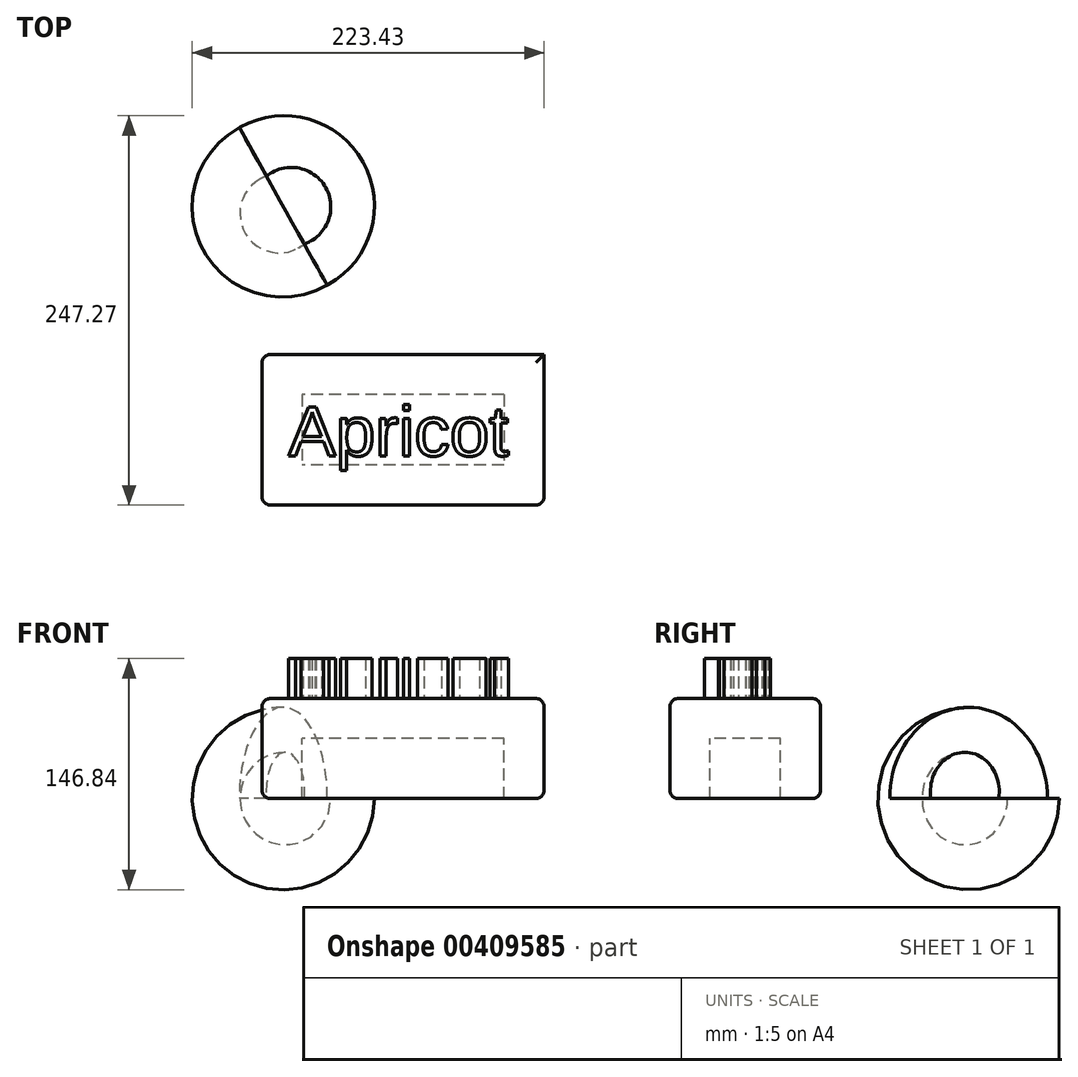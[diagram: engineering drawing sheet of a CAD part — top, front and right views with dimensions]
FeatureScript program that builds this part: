
annotation { "Feature Type Name" : "Feature", "Feature Type Description" : "" }
export const myFeature = defineFeature(function(context is Context, id is Id, definition is map)
    precondition{}
    {
        {
            var Q0;
            Q0=qCreatedBy(makeId("Top.planeOp"),FACE);
            var sketch = newSketch(context, id + "F0", { "sketchPlane" : qUnion([Q0])});
            skLineSegment(sketch, "E0.bottom", {"start": v(-97.09, -39.65) * mm, "end": v(81.91, -39.65) * mm});
            skLineSegment(sketch, "E0.top", {"start": v(-97.09, 55.98) * mm, "end": v(81.91, 55.98) * mm});
            skLineSegment(sketch, "E0.left", {"start": v(-97.09, -39.65) * mm, "end": v(-97.09, 55.98) * mm});
            skLineSegment(sketch, "E0.right", {"start": v(81.91, -39.65) * mm, "end": v(81.91, 55.98) * mm});
            skSolve(sketch);
        }
        {
            var Q0;
            Q0=makeQuery(id+"F0.imprint","IMPRINT",FACE,{"disambiguationData":[TD([[makeQuery(id+"F0.imprint","IMPRINT",EDGE,{"derivedFrom":sQuery(id+"F0.wireOp",EDGE,"E0.bottom")}),1.0]])]});
            extrude(context, id + "F1", {"entities" : qUnion([Q0]), "depth" : 63.5 * mm});
        }
        {
            var Q0;
            Q0=qCreatedBy(makeId("Top.planeOp"),FACE);
            var sketch = newSketch(context, id + "F2", { "sketchPlane" : qUnion([Q0])});
            skLineSegment(sketch, "E1", {"start": v(0, 0) * mm, "end": v(-111.55, 200.04) * mm});
            skArc(sketch, "E2", {"start": v(-55.78, 100.02) * mm, "mid": v(-33.06, 178.25) * mm, "end": v(-111.55, 200.04) * mm});
            skArc(sketch, "E3", {"start": v(-70.34, 126.14) * mm, "mid": v(-56.68, 161.99) * mm, "end": v(-94.36, 169.2) * mm});
            skSolve(sketch);
        }
        {
            var Q0;
            {var subQ0=sQuery(id+"F2.wireOp",EDGE,"E2");Q0=makeQuery(id+"F2.imprint","IMPRINT",FACE,{"disambiguationData":[TD([[makeQuery(id+"F2.imprint","IMPRINT",EDGE,{"derivedFrom":subQ0}),1.0]])]});}
            var Q1;
            Q1=sQuery(id+"F2.wireOp",EDGE,"E1");
            revolve(context, id + "F3", {"entities" : qUnion([Q0]), "axis" : qUnion([Q1]), "revolveType" : RevolveType.ONE_DIRECTION, "angle" : 270 * degree});
        }
        {
            var Q0;
            Q0=makeQuery(id+"F1.opExtrude","SWEPT_FACE",FACE,{"disambiguationData":[OSD([sQuery(id+"F0.wireOp",EDGE,"E0.bottom")])]});
            var Q1;
            Q1=makeQuery(id+"F1.opExtrude","SWEPT_FACE",FACE,{"disambiguationData":[OSD([sQuery(id+"F0.wireOp",EDGE,"E0.left")])]});
            var Q2;
            Q2=makeQuery(id+"F1.opExtrude","CAP_EDGE",EDGE,{"disambiguationData":[OSD([sQuery(id+"F0.wireOp",EDGE,"E0.right")])],"isStart":false});
            var Q3;
            Q3=makeQuery(id+"F1.opExtrude","CAP_FACE",FACE,{"disambiguationData":[OSD([sQuery(id+"F0.wireOp",EDGE,"E0.bottom"),sQuery(id+"F0.wireOp",EDGE,"E0.top"),sQuery(id+"F0.wireOp",EDGE,"E0.left"),sQuery(id+"F0.wireOp",EDGE,"E0.right")])],"isStart":false});
            var Q4;
            Q4=makeQuery(id+"F1.opExtrude","CAP_FACE",FACE,{"disambiguationData":[OSD([sQuery(id+"F0.wireOp",EDGE,"E0.bottom"),sQuery(id+"F0.wireOp",EDGE,"E0.top"),sQuery(id+"F0.wireOp",EDGE,"E0.left"),sQuery(id+"F0.wireOp",EDGE,"E0.right")])],"isStart":true});
            fillet(context, id + "F4", {"entities" : qUnion([Q0, Q1, Q2, Q3, Q4]), "radius" : 5.08 * mm, "tangentPropagation" : true, "allowEdgeOverflow" : false});
        }
        {
            var Q0;
            Q0=makeQuery(id+"F1.opExtrude","CAP_FACE",FACE,{"disambiguationData":[OSD([sQuery(id+"F0.wireOp",EDGE,"E0.bottom"),sQuery(id+"F0.wireOp",EDGE,"E0.top"),sQuery(id+"F0.wireOp",EDGE,"E0.left"),sQuery(id+"F0.wireOp",EDGE,"E0.right")])],"isStart":true});
            shell(context, id + "F5", {"entities" : qUnion([Q0]), "thickness" : 25.4 * mm});
        }
        {
            var Q0;
            Q0=makeQuery(id+"F1.opExtrude","CAP_FACE",FACE,{"disambiguationData":[OSD([sQuery(id+"F0.wireOp",EDGE,"E0.bottom"),sQuery(id+"F0.wireOp",EDGE,"E0.top"),sQuery(id+"F0.wireOp",EDGE,"E0.left"),sQuery(id+"F0.wireOp",EDGE,"E0.right")])],"isStart":false});
            var sketch = newSketch(context, id + "F6", { "sketchPlane" : qUnion([Q0])});
            skText(sketch, "E4", { "text": "Apricot", "fontName": "Arimo-Regular.ttf"});
            const initialGuessF6  = {"E4": [-0.0803, -0.00837, 1, 0, 0.03236]};
            skSetInitialGuess(sketch, initialGuessF6);
            skSolve(sketch);
        }
        {
            var Q0;
            Q0 = qSketchRegion(id + "F6", true);
            extrude(context, id + "F7", {"entities" : qUnion([Q0]), "operationType" : NewBodyOperationType.ADD, "depth" : 25.4 * mm});
        }
    });
